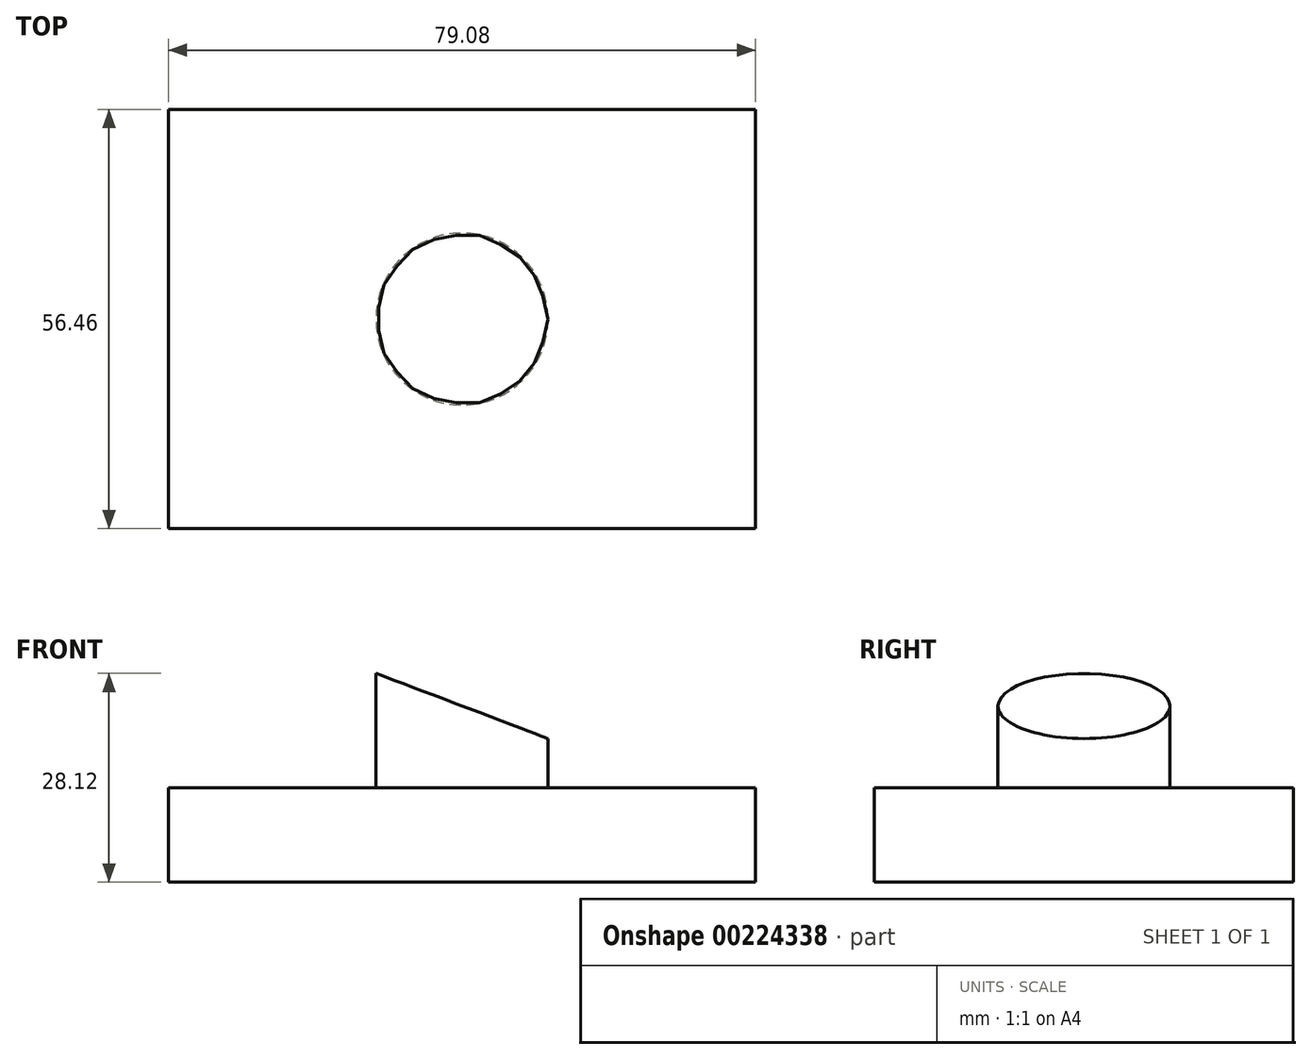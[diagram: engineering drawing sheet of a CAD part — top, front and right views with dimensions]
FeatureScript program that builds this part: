
annotation { "Feature Type Name" : "Feature", "Feature Type Description" : "" }
export const myFeature = defineFeature(function(context is Context, id is Id, definition is map)
    precondition{}
    {
        {
            var Q0;
            Q0=qCreatedBy(makeId("Top.planeOp"),FACE);
            var sketch = newSketch(context, id + "F0", { "sketchPlane" : qUnion([Q0])});
            skLineSegment(sketch, "E0.bottom", {"start": v(-39.54, 28.23) * mm, "end": v(39.54, 28.23) * mm});
            skLineSegment(sketch, "E0.top", {"start": v(-39.54, -28.23) * mm, "end": v(39.54, -28.23) * mm});
            skLineSegment(sketch, "E0.left", {"start": v(-39.54, 28.23) * mm, "end": v(-39.54, -28.23) * mm});
            skLineSegment(sketch, "E0.right", {"start": v(39.54, 28.23) * mm, "end": v(39.54, -28.23) * mm});
            skPoint(sketch, "E0.middle", {"position": v(0, 0) * mm});
            skSolve(sketch);
        }
        {
            var Q0;
            Q0=makeQuery(id+"F0.imprint","IMPRINT",FACE,{"disambiguationData":[TD([[makeQuery(id+"F0.imprint","IMPRINT",EDGE,{"derivedFrom":sQuery(id+"F0.wireOp",EDGE,"E0.bottom")}),-1.0]])]});
            extrude(context, id + "F1", {"entities" : qUnion([Q0]), "depth" : 12.7 * mm});
        }
        {
            var Q0;
            Q0=makeQuery(id+"F1.opExtrude","CAP_FACE",FACE,{"disambiguationData":[OSD([sQuery(id+"F0.wireOp",EDGE,"E0.bottom"),sQuery(id+"F0.wireOp",EDGE,"E0.top"),sQuery(id+"F0.wireOp",EDGE,"E0.left"),sQuery(id+"F0.wireOp",EDGE,"E0.right")])],"isStart":false});
            var sketch = newSketch(context, id + "F2", { "sketchPlane" : qUnion([Q0])});
            skCircle(sketch, "E1", {"center": v(0, 0) * mm, "radius": 11.59 * mm});
            skSolve(sketch);
        }
        {
            var Q0;
            Q0=makeQuery(id+"F2.imprint","IMPRINT",FACE,{"disambiguationData":[TD([[makeQuery(id+"F2.imprint","IMPRINT",EDGE,{"derivedFrom":sQuery(id+"F2.wireOp",EDGE,"E1")}),1.0]])]});
            extrude(context, id + "F3", {"entities" : qUnion([Q0]), "operationType" : NewBodyOperationType.ADD, "depth" : 23.37 * mm});
        }
        {
            var Q0;
            Q0=qCreatedBy(makeId("Front.planeOp"),FACE);
            var sketch = newSketch(context, id + "F4", { "sketchPlane" : qUnion([Q0])});
            skLineSegment(sketch, "E2", {"start": v(-16.65, 30.04) * mm, "end": v(12.73, 18.9) * mm});
            skLineSegment(sketch, "E3", {"start": v(12.73, 18.9) * mm, "end": v(12.73, 45.34) * mm});
            skLineSegment(sketch, "E4", {"start": v(12.73, 45.34) * mm, "end": v(-16.65, 45.34) * mm});
            skLineSegment(sketch, "E5", {"start": v(-16.65, 45.34) * mm, "end": v(-16.65, 30.04) * mm});
            skSolve(sketch);
        }
        {
            var Q0;
            Q0=makeQuery(id+"F4.imprint","IMPRINT",FACE,{"disambiguationData":[TD([[makeQuery(id+"F4.imprint","IMPRINT",EDGE,{"derivedFrom":sQuery(id+"F4.wireOp",EDGE,"E2")}),1.0]])]});
            extrude(context, id + "F5", {"entities" : qUnion([Q0]), "operationType" : NewBodyOperationType.REMOVE, "oppositeDirection" : true, "depth" : 20.83 * mm});
        }
        {
            var Q0;
            Q0 = qSketchRegion(id + "F4", true);
            extrude(context, id + "F6", {"entities" : qUnion([Q0]), "operationType" : NewBodyOperationType.REMOVE, "depth" : 37.34 * mm});
        }
    });
